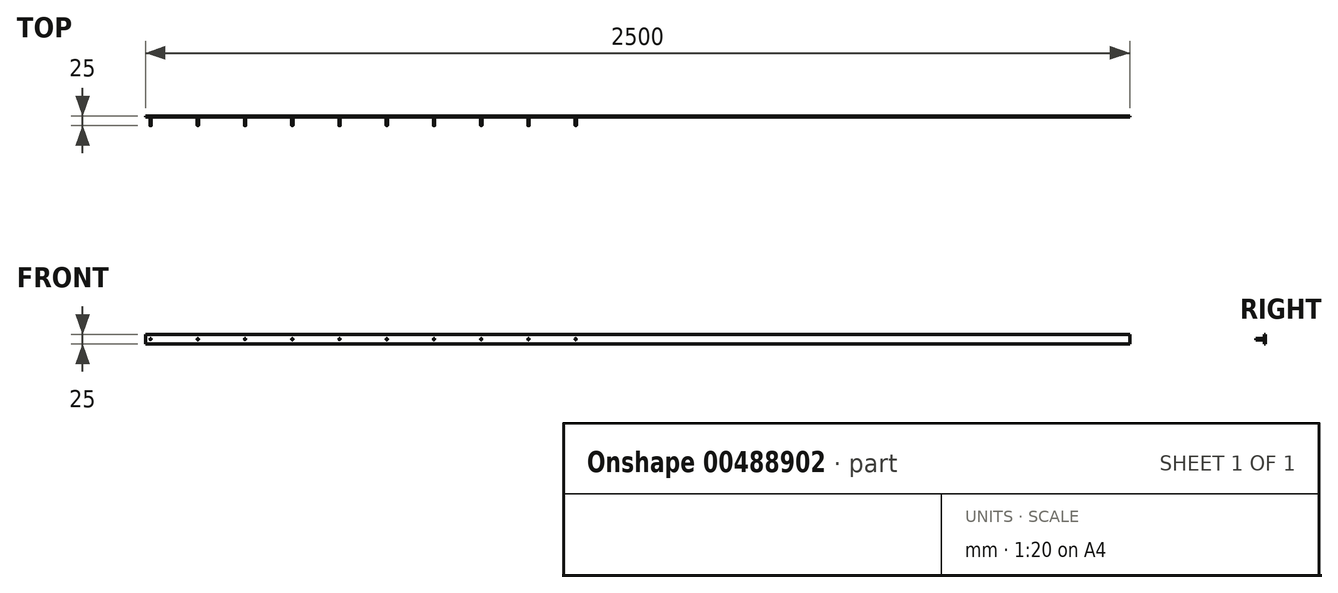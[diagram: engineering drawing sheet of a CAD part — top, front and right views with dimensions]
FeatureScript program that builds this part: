
annotation { "Feature Type Name" : "Feature", "Feature Type Description" : "" }
export const myFeature = defineFeature(function(context is Context, id is Id, definition is map)
    precondition{}
    {
        {
            var Q0;
            Q0=qCreatedBy(makeId("Front.planeOp"),FACE);
            var sketch = newSketch(context, id + "F0", { "sketchPlane" : qUnion([Q0])});
            skLineSegment(sketch, "E0.bottom", {"start": v(-1044.21, -0.29) * mm, "end": v(1455.79, -0.29) * mm});
            skLineSegment(sketch, "E0.top", {"start": v(-1044.21, 24.71) * mm, "end": v(1455.79, 24.71) * mm});
            skLineSegment(sketch, "E0.left", {"start": v(-1044.21, -0.29) * mm, "end": v(-1044.21, 24.71) * mm});
            skLineSegment(sketch, "E0.right", {"start": v(1455.79, -0.29) * mm, "end": v(1455.79, 24.71) * mm});
            skCircle(sketch, "E1", {"center": v(-1031.71, 12.21) * mm, "radius": 1.5 * mm});
            skCircle(sketch, "E2.1.0.0", {"center": v(-911.71, 12.21) * mm, "radius": 1.5 * mm});
            skCircle(sketch, "E2.2.0.0", {"center": v(-791.71, 12.21) * mm, "radius": 1.5 * mm});
            skCircle(sketch, "E2.3.0.0", {"center": v(-671.71, 12.21) * mm, "radius": 1.5 * mm});
            skCircle(sketch, "E2.4.0.0", {"center": v(-551.71, 12.21) * mm, "radius": 1.5 * mm});
            skCircle(sketch, "E2.5.0.0", {"center": v(-431.71, 12.21) * mm, "radius": 1.5 * mm});
            skCircle(sketch, "E2.6.0.0", {"center": v(-311.71, 12.21) * mm, "radius": 1.5 * mm});
            skCircle(sketch, "E2.7.0.0", {"center": v(-191.71, 12.21) * mm, "radius": 1.5 * mm});
            skCircle(sketch, "E2.8.0.0", {"center": v(-71.71, 12.21) * mm, "radius": 1.5 * mm});
            skCircle(sketch, "E2.9.0.0", {"center": v(48.29, 12.21) * mm, "radius": 1.5 * mm});
            skLineSegment(sketch, "E2.direction1", {"start": v(-1031.71, 12.21) * mm, "end": v(-911.71, 12.21) * mm, "construction": true});
            skSolve(sketch);
        }
        {
            var Q0;
            Q0 = qSketchRegion(id + "F0", true);
            extrude(context, id + "F1", {"entities" : qUnion([Q0]), "depth" : 3 * mm});
        }
        {
            var Q0;
            Q0=makeQuery(id+"F0.imprint","IMPRINT",FACE,{"disambiguationData":[TD([[makeQuery(id+"F0.imprint","IMPRINT",EDGE,{"derivedFrom":sQuery(id+"F0.wireOp",EDGE,"E1")}),1.0]])]});
            var Q1;
            Q1=makeQuery(id+"F0.imprint","IMPRINT",FACE,{"disambiguationData":[TD([[makeQuery(id+"F0.imprint","IMPRINT",EDGE,{"derivedFrom":sQuery(id+"F0.wireOp",EDGE,"E2.1.0.0")}),1.0]])]});
            var Q2;
            Q2=makeQuery(id+"F0.imprint","IMPRINT",FACE,{"disambiguationData":[TD([[makeQuery(id+"F0.imprint","IMPRINT",EDGE,{"derivedFrom":sQuery(id+"F0.wireOp",EDGE,"E2.2.0.0")}),1.0]])]});
            var Q3;
            Q3=makeQuery(id+"F0.imprint","IMPRINT",FACE,{"disambiguationData":[TD([[makeQuery(id+"F0.imprint","IMPRINT",EDGE,{"derivedFrom":sQuery(id+"F0.wireOp",EDGE,"E2.3.0.0")}),1.0]])]});
            var Q4;
            Q4=makeQuery(id+"F0.imprint","IMPRINT",FACE,{"disambiguationData":[TD([[makeQuery(id+"F0.imprint","IMPRINT",EDGE,{"derivedFrom":sQuery(id+"F0.wireOp",EDGE,"E2.4.0.0")}),1.0]])]});
            var Q5;
            Q5=makeQuery(id+"F0.imprint","IMPRINT",FACE,{"disambiguationData":[TD([[makeQuery(id+"F0.imprint","IMPRINT",EDGE,{"derivedFrom":sQuery(id+"F0.wireOp",EDGE,"E2.5.0.0")}),1.0]])]});
            var Q6;
            Q6=makeQuery(id+"F0.imprint","IMPRINT",FACE,{"disambiguationData":[TD([[makeQuery(id+"F0.imprint","IMPRINT",EDGE,{"derivedFrom":sQuery(id+"F0.wireOp",EDGE,"E2.6.0.0")}),1.0]])]});
            var Q7;
            Q7=makeQuery(id+"F0.imprint","IMPRINT",FACE,{"disambiguationData":[TD([[makeQuery(id+"F0.imprint","IMPRINT",EDGE,{"derivedFrom":sQuery(id+"F0.wireOp",EDGE,"E2.7.0.0")}),1.0]])]});
            var Q8;
            Q8=makeQuery(id+"F0.imprint","IMPRINT",FACE,{"disambiguationData":[TD([[makeQuery(id+"F0.imprint","IMPRINT",EDGE,{"derivedFrom":sQuery(id+"F0.wireOp",EDGE,"E2.8.0.0")}),1.0]])]});
            var Q9;
            Q9=makeQuery(id+"F0.imprint","IMPRINT",FACE,{"disambiguationData":[TD([[makeQuery(id+"F0.imprint","IMPRINT",EDGE,{"derivedFrom":sQuery(id+"F0.wireOp",EDGE,"E2.9.0.0")}),1.0]])]});
            extrude(context, id + "F2", {"entities" : qUnion([Q0, Q1, Q2, Q3, Q4, Q5, Q6, Q7, Q8, Q9]), "operationType" : NewBodyOperationType.ADD, "depth" : 25 * mm});
        }
    });
